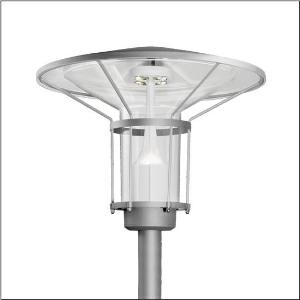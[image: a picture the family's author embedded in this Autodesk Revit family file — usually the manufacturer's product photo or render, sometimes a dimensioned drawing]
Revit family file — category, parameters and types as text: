
# Revit family: laterne_classic_iq___st1_2a_5xa5245ef14h_7fcb
name_source: partatom
category: Lighting Fixtures
units: mm (PartAtom-declared; Revit-internal decimal feet)

## family parameters
Cut with Voids When Loaded = No
Host = Face
Light Source = No
Part Type = Normal
Room Calculation Point = No
Round Connector Dimension = Use Diameter
Shared = No

## types (1)
- --- (1 x LED, 1380 lm, 10.5 W, 3000K)
    Apparent Load = 11 VA
    CIE Flux Codes = 21 60 93 97 100
    Color Rendering = 70
    Color Temperature = 3000K
    Default Elevation = 1800 mm
    Description = Lantern Classic iQ, mast luminaire, Module 540 iQ-SR, primary light control with 3 zone facetted reflector, of plastic, silver coated, highly specular, structured, primary optical cover: cover, of PMMA, transparent, light distribution: ST1.2a, light emission: direct distribution, primary light characteristic: asymmetric, installation type: post-top, LED, High Power LED, rated luminous flux: 1.380lm, luminous efficacy: 131lm/W, light colour: 730, colour temperature: 3000K, control gear: ECG iQ, control: Auto-Match, Temp-Guard, Lumen-Switch, Night-Set, Smart-Wire, Light-Fading, Desk-Remote (wireless, voltage-free reading and setting of iQ features in the workshop via application-optimized NFC function/RFID function), optimised constant luminous flux control (CLO 2.0), Street-Remote, presetting dimming logarithmic, with terminal, 6-pole, max. 2.5mm², mains connection: 230..240V, AC, 50/60Hz, start of lifetime: 11W, end of service life: 11W, reduction: 5W, luminaire housing, upper part, of glass-fibre reinforced polyester, coated, Siteco® metallic grey (DB 702S), diameter: 750mm, height: 596mm, spigot size: d x l = 76 x 70mm (post-top) | with reducer (optional accessory) 60 x 70mm, post-top mast mounting element, of diecast aluminium, coated, Siteco® metallic grey (DB 702S), Module 540 iQ-SR, traffic white (RAL 9016), equipment: standard, protection rating (complete): IP65, insulation class (complete): insulation class II (safety insulation), certification: CE, ENEC, VDE, packaging unit: 1 piece

Light Distribution: ST1.2a
    Height = 596 mm
    Lamp = 1 x LED
    Lamp Light Flux = 1380 lm
    Lamp Power = 10.5 W
    Lamp count = 1
    Length = 750 mm
    Luminous efficacy = 131 lm/W
    Manufacturer = Siteco
    ModVariant = No
    Model = 5XA5245EF14H
    Number of Poles = 1
    OnlyDefault = Yes
    Power Factor = 1
    Product Name = Laterne Classic iQ | ST1.2a
    Product group = mast luminaire | pylon top
    ProductGroupID = 6100
    Protection Class = Protection class II
    Protection Degree = IP 65
    RLX_Detail_Level = 1
    RLX_Emergency_Light_Flux = 0 lm
    RLX_Emergency_Type = 0
    RLX_Emergency_Type_DB = No
    RlxData = <blob elided: 91453 chars, md5=7b912b97>
    Socket = socket
    Standby Power = 0 W
    System Light Flux = 1380 lm
    System Power = 11 W
    Type Comments = factory setting: luminous flux: 100 % | dim-lin: 254 | 419 mA
    Type Image = l_1006052.jpg
    URL = http://relux.com
    VarID = @adj_092699
    Voltage = 0 V
    Weight = 0.00 kg
    Width = 0 mm  [stored 0 ft]

note: [stored X ft] marks values corroborated as IEEE doubles in the binary element streams (Revit-internal decimal feet)

## geometry (parser evidence)
native form markers: Blend x4, Sweep x14
no freeform markers — native parametric forms only
